# Revit family: Console Lavatory_TOTO_L4706
name_source: partatom
category: 衛生器具
revit_build: Autodesk Revit 2018 (Build: 20181011_1500(x64)
units: mm (PartAtom-declared; Revit-internal decimal feet)

## family parameters
OmniClass タイトル = Sanitary, Laundry, and Cleaning Equipment
OmniClass 番号 = 23.45.00.00
パーツ タイプ = 標準
ロード時にボイドで切り取り = いいえ
丸型コネクタ寸法 = 直径を使用
作業面ベース = いいえ
共有 = いいえ
常に垂直 = はい
部屋計算ポイント = いいえ

## types (1)
- Console Lavatory_TOTO_L4706
    Ceramic = TOTO_Ceramic
    Chrome = Chrome
    Height = 117  [stored 0.383858 ft]
    Length = 420  [stored 1.37795 ft]
    TOTO asiaoceania = L4706E
    TOTO asiaoceania URL = http://asia.toto.com
    TOTO china = LW4706B
    TOTO china URL = http://www.toto.com.cn
    TOTO hongkong = L4706E
    TOTO hongkong URL = http://hk.toto.com
    TOTO india = L4706E
    TOTO india URL = https://in.toto.com
    TOTO taiwan = L4706E
    TOTO taiwan URL = https://www.twtoto.com.tw
    TOTO thailand = LW4706
    TOTO thailand URL = https://th.toto.com
    TOTO vietnam = LT4706
    TOTO vietnam URL = https://vn.toto.com
    Width = 600
    製造元 = TOTO LTD.
    説明 = Console Lavatory

note: [stored X ft] marks values corroborated as IEEE doubles in the binary element streams (Revit-internal decimal feet)
